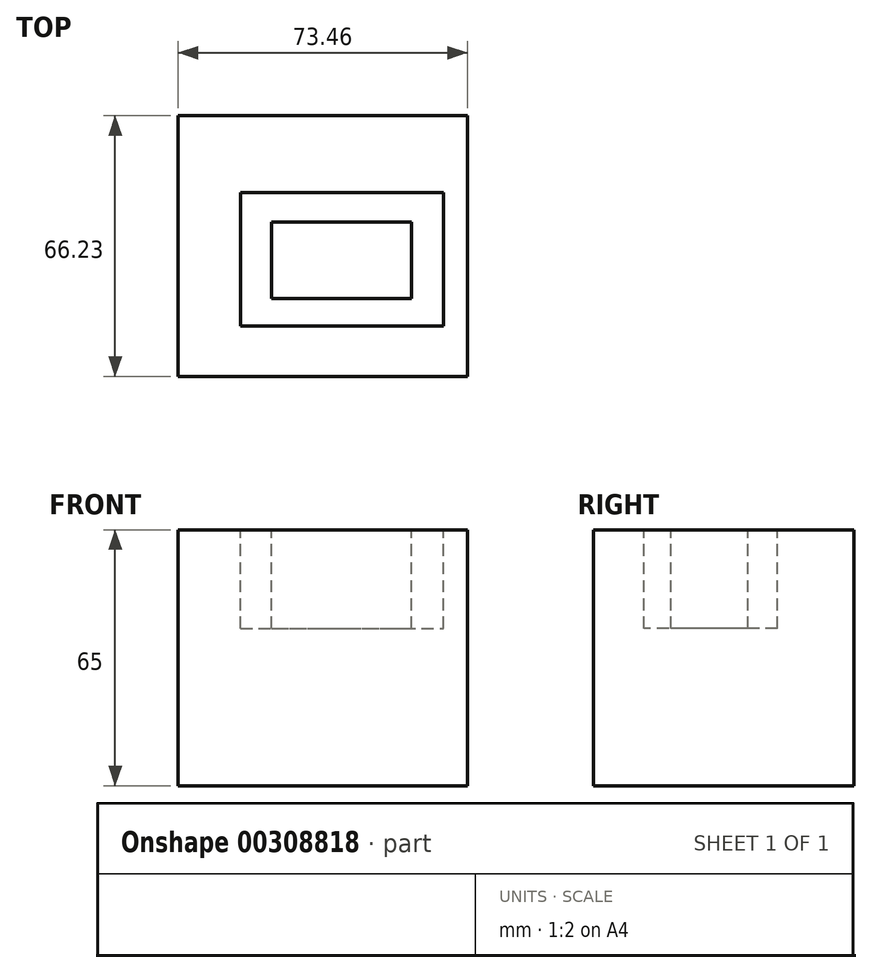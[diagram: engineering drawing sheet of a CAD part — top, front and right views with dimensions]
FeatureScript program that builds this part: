
annotation { "Feature Type Name" : "Feature", "Feature Type Description" : "" }
export const myFeature = defineFeature(function(context is Context, id is Id, definition is map)
    precondition{}
    {
        {
            var Q0;
            Q0=qCreatedBy(makeId("Top.planeOp"),FACE);
            var sketch = newSketch(context, id + "F0", { "sketchPlane" : qUnion([Q0])});
            skLineSegment(sketch, "E0.bottom", {"start": v(-23.65, 27) * mm, "end": v(49.81, 27) * mm});
            skLineSegment(sketch, "E0.top", {"start": v(-23.65, -39.24) * mm, "end": v(49.81, -39.24) * mm});
            skLineSegment(sketch, "E0.left", {"start": v(-23.65, 27) * mm, "end": v(-23.65, -39.24) * mm});
            skLineSegment(sketch, "E0.right", {"start": v(49.81, 27) * mm, "end": v(49.81, -39.24) * mm});
            skSolve(sketch);
        }
        {
            var Q0;
            Q0=makeQuery(id+"F0.imprint","IMPRINT",FACE,{"disambiguationData":[TD([[makeQuery(id+"F0.imprint","IMPRINT",EDGE,{"derivedFrom":sQuery(id+"F0.wireOp",EDGE,"E0.bottom")}),-1.0]])]});
            extrude(context, id + "F1", {"entities" : qUnion([Q0]), "depth" : 65 * mm});
        }
        {
            var Q0;
            Q0=makeQuery(id+"F1.opExtrude","CAP_FACE",FACE,{"disambiguationData":[OSD([sQuery(id+"F0.wireOp",EDGE,"E0.bottom"),sQuery(id+"F0.wireOp",EDGE,"E0.top"),sQuery(id+"F0.wireOp",EDGE,"E0.left"),sQuery(id+"F0.wireOp",EDGE,"E0.right")])],"isStart":false});
            var sketch = newSketch(context, id + "F2", { "sketchPlane" : qUnion([Q0])});
            skLineSegment(sketch, "E1.bottom", {"start": v(-7.8, 7.51) * mm, "end": v(43.69, 7.51) * mm});
            skLineSegment(sketch, "E1.top", {"start": v(-7.8, -26.44) * mm, "end": v(43.69, -26.44) * mm});
            skLineSegment(sketch, "E1.left", {"start": v(-7.8, 7.51) * mm, "end": v(-7.8, -26.44) * mm});
            skLineSegment(sketch, "E1.right", {"start": v(43.69, 7.51) * mm, "end": v(43.69, -26.44) * mm});
            skLineSegment(sketch, "E2.bottom", {"start": v(0, 0) * mm, "end": v(35.62, 0) * mm});
            skLineSegment(sketch, "E2.top", {"start": v(0, -19.48) * mm, "end": v(35.62, -19.48) * mm});
            skLineSegment(sketch, "E2.left", {"start": v(0, 0) * mm, "end": v(0, -19.48) * mm});
            skLineSegment(sketch, "E2.right", {"start": v(35.62, 0) * mm, "end": v(35.62, -19.48) * mm});
            skSolve(sketch);
        }
        {
            var Q0;
            Q0=makeQuery(id+"F2.imprint","IMPRINT",FACE,{"disambiguationData":[TD([[makeQuery(id+"F2.imprint","IMPRINT",EDGE,{"derivedFrom":sQuery(id+"F2.wireOp",EDGE,"E1.bottom")}),-1.0]])]});
            extrude(context, id + "F3", {"entities" : qUnion([Q0]), "operationType" : NewBodyOperationType.REMOVE, "oppositeDirection" : true, "depth" : 25 * mm});
        }
    });
